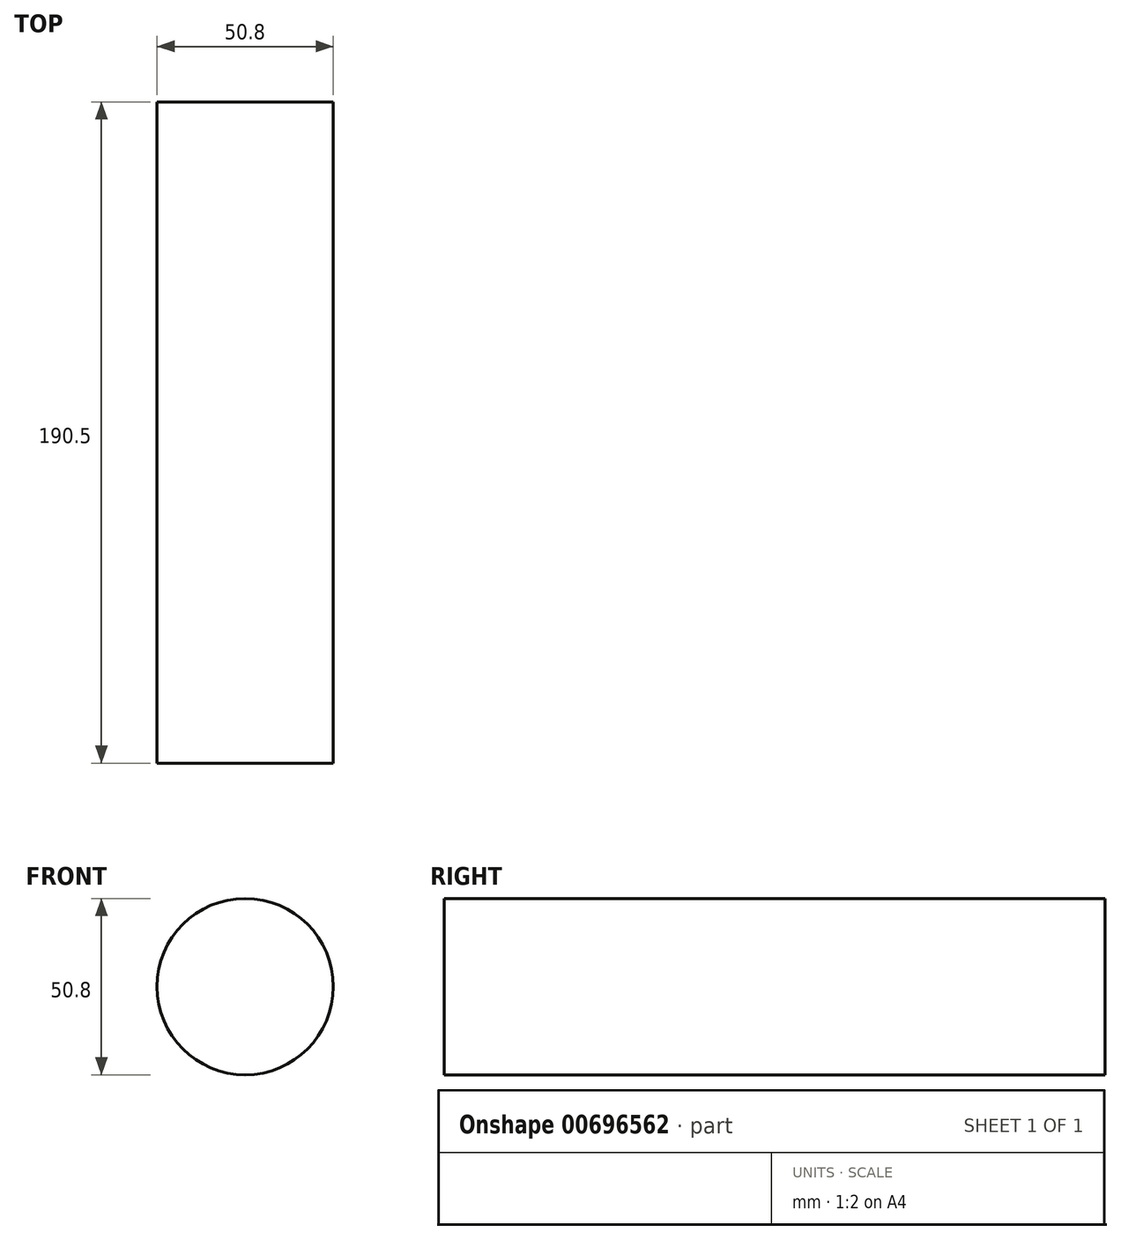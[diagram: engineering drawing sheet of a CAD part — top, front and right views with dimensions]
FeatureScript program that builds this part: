
annotation { "Feature Type Name" : "Feature", "Feature Type Description" : "" }
export const myFeature = defineFeature(function(context is Context, id is Id, definition is map)
    precondition{}
    {
        {
            var Q0;
            Q0=qCreatedBy(makeId("Front.planeOp"),FACE);
            var sketch = newSketch(context, id + "F0", { "sketchPlane" : qUnion([Q0])});
            skCircle(sketch, "E0", {"center": v(0, 0) * mm, "radius": 25.4 * mm});
            skSolve(sketch);
        }
        {
            var Q0;
            Q0 = qSketchRegion(id + "F0", true);
            extrude(context, id + "F1", {"entities" : qUnion([Q0]), "depth" : 190.5 * mm, "offsetDistance" : 25.4 * mm});
        }
    });
